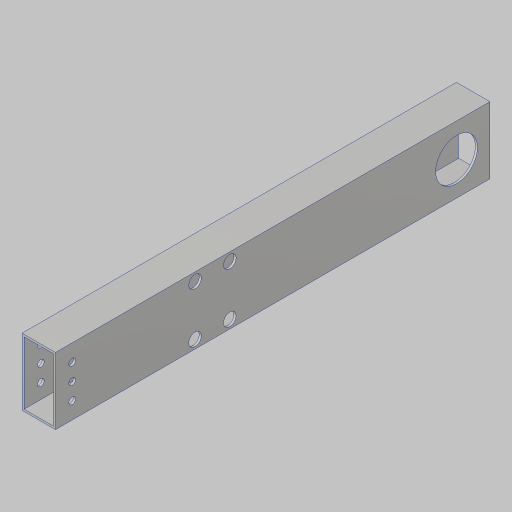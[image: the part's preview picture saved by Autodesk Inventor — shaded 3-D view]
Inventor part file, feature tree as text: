
AUTODESK INVENTOR PART (.ipt)
format: ipt  version: 2023.5 (Build 275446000, 446)  size: 174,080 bytes
history: native  units: in
note: dims shown in document units (in); Inventor stores cm internally (conversion verified against a paired STEP export)
features: projected_geometry x5, sketch x4, hole x3, extrude x2
ambient origin geometry x8: Origin, YZ Plane, XZ Plane, XY Plane, X Axis, Y Axis, Z Axis, Center Point
bodies: Solid1 (feature_tree)
feature tree (14):
  extrude  "Extrusion1"  Depth=1.25in
  extrude  "Extrusion3"  TaperAngle=0.0deg  [1 undecoded]
  hole  "Hole1"  [1 undecoded]
  hole  "Hole3"  [1 undecoded]
  hole  "Hole4"  [1 undecoded]
  sketch  "Sketch3"  dims[d4=0.0in d8=1.25in]
  sketch  "Sketch4"  dims[d9=1.0in d10=0.0in d11=0.0in]
  sketch  "Sketch6"  dims[d12=0.5in d13=0.5in]
  sketch  "Sketch7"  dims[d14=0.5in d15=0.201in d16=0.75in d17=0.385in d18=0.25in d19=0.5635in d20=1.0in d21=0.8108in d35=6.0in d36=0.3793in d37=8.0in d38=2.0in d39=0.378in d40=0.5in d41=0.375in d42=0.75in d43=0.385in d44=0.25in d45=0.5635in d46=1.0in d47=0.8108in d48=6.0in d49=8.0in d50=2.0in d51=0.3793in d52=0.378in d53=0.5in d54=0.375in d55=0.75in d56=0.375in d57=0.25in d58=0.5635in d59=1.0in d60=0.8108in]
  projected_geometry  "Projected Loop3"
  projected_geometry  "Project Cut Edges1"
  projected_geometry  "Project Cut Edges3"
  projected_geometry  "Project Cut Edges4"
  projected_geometry  "Project Cut Edges5"
note: 4 required parameter values undecoded (feature->parameter linkage not recoverable at this tier; creation-order binding heuristic only, values carry confidence <= 0.55)
